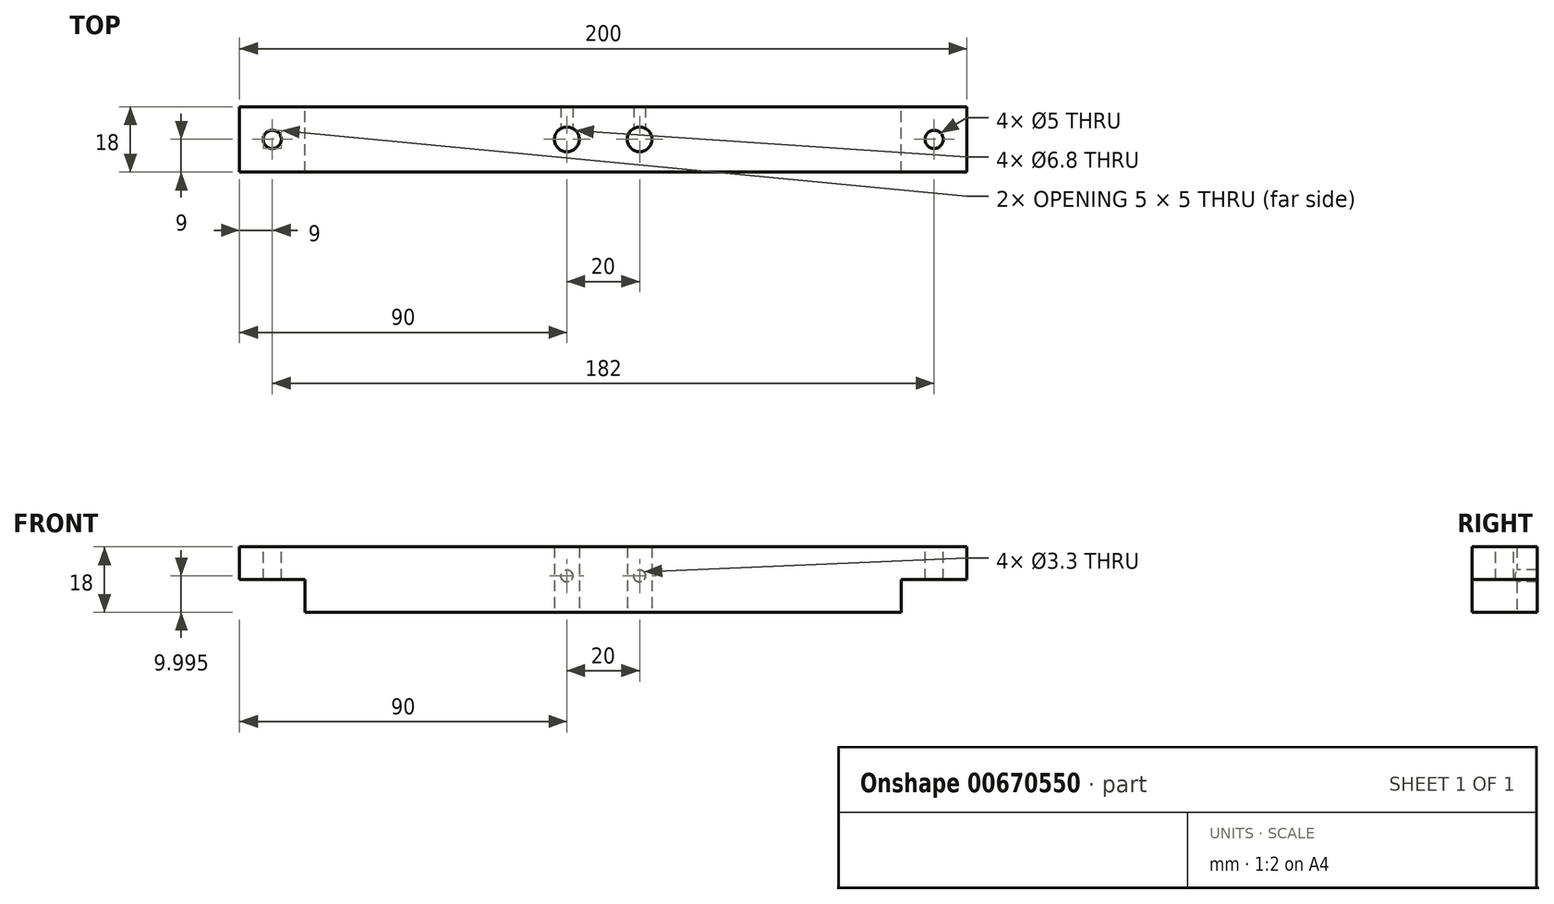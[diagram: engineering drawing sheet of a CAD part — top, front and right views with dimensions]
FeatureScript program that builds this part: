
annotation { "Feature Type Name" : "Feature", "Feature Type Description" : "" }
export const myFeature = defineFeature(function(context is Context, id is Id, definition is map)
    precondition{}
    {
        {
            var Q0;
            Q0=qCreatedBy(makeId("Right.planeOp"),FACE);
            var sketch = newSketch(context, id + "F0", { "sketchPlane" : qUnion([Q0])});
            skLineSegment(sketch, "E0.bottom", {"start": v(5.9, 10.36) * mm, "end": v(-12.1, 10.36) * mm});
            skLineSegment(sketch, "E0.top", {"start": v(5.9, -7.64) * mm, "end": v(-12.1, -7.64) * mm});
            skLineSegment(sketch, "E0.left", {"start": v(5.9, 10.36) * mm, "end": v(5.9, -7.64) * mm});
            skLineSegment(sketch, "E0.right", {"start": v(-12.1, 10.36) * mm, "end": v(-12.1, -7.64) * mm});
            skSolve(sketch);
        }
        {
            var Q0;
            Q0=makeQuery(id+"F0.imprint","IMPRINT",FACE,{"disambiguationData":[TD([[makeQuery(id+"F0.imprint","IMPRINT",EDGE,{"derivedFrom":sQuery(id+"F0.wireOp",EDGE,"E0.bottom")}),1.0]])]});
            extrude(context, id + "F1", {"entities" : qUnion([Q0]), "depth" : 200 * mm, "offsetDistance" : 25 * mm, "symmetric" : true});
        }
        {
            var Q0;
            Q0=makeQuery(id+"F1.opExtrude","SWEPT_FACE",FACE,{"disambiguationData":[OSD([sQuery(id+"F0.wireOp",EDGE,"E0.bottom")])]});
            var sketch = newSketch(context, id + "F2", { "sketchPlane" : qUnion([Q0])});
            skPoint(sketch, "E1", {"position": v(-10, -3.1) * mm});
            skPoint(sketch, "E2", {"position": v(10, -3.1) * mm});
            skSolve(sketch);
        }
        {
            var Q0;
            Q0=sQuery(id+"F2.wireOp",VERTEX,"E1");
            var Q1;
            Q1=sQuery(id+"F2.wireOp",VERTEX,"E2");
            var Q2;
            Q2=makeQuery(id+"F1.opExtrude","SWEPT_BODY",BODY,{"disambiguationData":[OSD([sQuery(id+"F0.wireOp",EDGE,"E0.bottom"),sQuery(id+"F0.wireOp",EDGE,"E0.top"),sQuery(id+"F0.wireOp",EDGE,"E0.left"),sQuery(id+"F0.wireOp",EDGE,"E0.right")])]});
            hole(context, id + "F3", {"style" : HoleStyle.SIMPLE, "endStyle" : HoleEndStyle.THROUGH, "standardTappedOrClearance" : lookupTablePath({ "standard" : "ISO", "engagement" : "75%", "pitch" : "1.25 mm", "size" : "M8", "type" : "Tapped" }), "standardBlindInLast" : lookupTablePath({ "standard" : "ISO", "engagement" : "75%", "pitch" : "1.25 mm", "size" : "M8", "type" : "Tapped" }), "holeDiameter" : 6.8 * mm, "majorDiameter" : 8 * mm, "showTappedDepth" : true, "isTappedThrough" : true, "tappedDepth" : 10 * mm, "tapClearance" : 3, "locations" : qUnion([Q0, Q1]), "scope" : qUnion([Q2]), "startStyle" : HoleStartStyle.PART});
        }
        {
            var Q0;
            Q0=makeQuery(id+"F1.opExtrude","SWEPT_FACE",FACE,{"disambiguationData":[OSD([sQuery(id+"F0.wireOp",EDGE,"E0.left")])]});
            var sketch = newSketch(context, id + "F4", { "sketchPlane" : qUnion([Q0])});
            skPoint(sketch, "E3", {"position": v(-10, 2.36) * mm});
            skPoint(sketch, "E4", {"position": v(10, 2.36) * mm});
            skSolve(sketch);
        }
        {
            var Q0;
            Q0=sQuery(id+"F4.wireOp",VERTEX,"E3");
            var Q1;
            Q1=sQuery(id+"F4.wireOp",VERTEX,"E4");
            var Q2;
            Q2=makeQuery(id+"F1.opExtrude","SWEPT_BODY",BODY,{"disambiguationData":[OSD([sQuery(id+"F0.wireOp",EDGE,"E0.bottom"),sQuery(id+"F0.wireOp",EDGE,"E0.top"),sQuery(id+"F0.wireOp",EDGE,"E0.left"),sQuery(id+"F0.wireOp",EDGE,"E0.right")])]});
            hole(context, id + "F5", {"style" : HoleStyle.SIMPLE, "endStyle" : HoleEndStyle.BLIND, "standardTappedOrClearance" : lookupTablePath({ "standard" : "ISO", "engagement" : "75%", "pitch" : "0.7 mm", "size" : "M4", "type" : "Tapped" }), "standardBlindInLast" : lookupTablePath({ "standard" : "ISO", "engagement" : "75%", "pitch" : "0.7 mm", "size" : "M4", "type" : "Tapped" }), "holeDiameter" : 3.3 * mm, "majorDiameter" : 4 * mm, "showTappedDepth" : true, "holeDepth" : 8 * mm, "isTappedThrough" : true, "tappedDepth" : 5.9 * mm, "tapClearance" : 3, "locations" : qUnion([Q0, Q1]), "scope" : qUnion([Q2]), "startStyle" : HoleStartStyle.PART});
        }
        {
            var Q0;
            Q0=makeQuery(id+"F1.opExtrude","SWEPT_FACE",FACE,{"disambiguationData":[OSD([sQuery(id+"F0.wireOp",EDGE,"E0.bottom")])]});
            var sketch = newSketch(context, id + "F6", { "sketchPlane" : qUnion([Q0])});
            skLineSegment(sketch, "E5.bottom", {"start": v(112, -12.1) * mm, "end": v(100, -12.1) * mm});
            skLineSegment(sketch, "E5.top", {"start": v(112, 5.9) * mm, "end": v(100, 5.9) * mm});
            skLineSegment(sketch, "E5.left", {"start": v(100, -12.1) * mm, "end": v(100, 5.9) * mm});
            skLineSegment(sketch, "E6.bottom", {"start": v(-100, -12.1) * mm, "end": v(-112, -12.1) * mm});
            skLineSegment(sketch, "E6.top", {"start": v(-100, 5.9) * mm, "end": v(-112, 5.9) * mm});
            skLineSegment(sketch, "E6.right", {"start": v(-100, -12.1) * mm, "end": v(-100, 5.9) * mm});
            skSolve(sketch);
        }
        {
            var Q0;
            Q0=makeQuery(id+"F1.opExtrude","SWEPT_FACE",FACE,{"disambiguationData":[OSD([sQuery(id+"F0.wireOp",EDGE,"E0.top")])]});
            var sketch = newSketch(context, id + "F7", { "sketchPlane" : qUnion([Q0])});
            skLineSegment(sketch, "E7.bottom", {"start": v(-100, 12.1) * mm, "end": v(-82, 12.1) * mm});
            skLineSegment(sketch, "E7.top", {"start": v(-100, -5.9) * mm, "end": v(-82, -5.9) * mm});
            skLineSegment(sketch, "E7.left", {"start": v(-100, 12.1) * mm, "end": v(-100, -5.9) * mm});
            skLineSegment(sketch, "E7.right", {"start": v(-82, 12.1) * mm, "end": v(-82, -5.9) * mm});
            skLineSegment(sketch, "E8.bottom", {"start": v(82, 12.1) * mm, "end": v(100, 12.1) * mm});
            skLineSegment(sketch, "E8.top", {"start": v(82, -5.9) * mm, "end": v(100, -5.9) * mm});
            skLineSegment(sketch, "E8.left", {"start": v(82, 12.1) * mm, "end": v(82, -5.9) * mm});
            skLineSegment(sketch, "E8.right", {"start": v(100, 12.1) * mm, "end": v(100, -5.9) * mm});
            skPoint(sketch, "E9", {"position": v(91, 3.1) * mm});
            skPoint(sketch, "E10", {"position": v(-91, 3.1) * mm});
            skSolve(sketch);
        }
        {
            var Q0;
            Q0=sQuery(id+"F7.wireOp",VERTEX,"E9");
            var Q1;
            Q1=sQuery(id+"F7.wireOp",VERTEX,"E10");
            var Q2;
            Q2=makeQuery(id+"F1.opExtrude","SWEPT_BODY",BODY,{"disambiguationData":[OSD([sQuery(id+"F0.wireOp",EDGE,"E0.bottom"),sQuery(id+"F0.wireOp",EDGE,"E0.top"),sQuery(id+"F0.wireOp",EDGE,"E0.left"),sQuery(id+"F0.wireOp",EDGE,"E0.right")])]});
            hole(context, id + "F8", {"style" : HoleStyle.SIMPLE, "endStyle" : HoleEndStyle.BLIND, "standardTappedOrClearance" : lookupTablePath({ "standard" : "ISO", "engagement" : "75%", "pitch" : "1 mm", "size" : "M6", "type" : "Tapped" }), "standardBlindInLast" : lookupTablePath({ "standard" : "ISO", "engagement" : "75%", "pitch" : "1 mm", "size" : "M6", "type" : "Tapped" }), "holeDiameter" : 5 * mm, "majorDiameter" : 6 * mm, "showTappedDepth" : true, "holeDepth" : 18 * mm, "isTappedThrough" : true, "tappedDepth" : 15 * mm, "tapClearance" : 3, "locations" : qUnion([Q0, Q1]), "scope" : qUnion([Q2]), "startStyle" : HoleStartStyle.PART});
        }
        {
            var Q0;
            Q0=makeQuery(id+"F7.imprint","IMPRINT",FACE,{"disambiguationData":[TD([[makeQuery(id+"F7.imprint","IMPRINT",EDGE,{"derivedFrom":sQuery(id+"F7.wireOp",EDGE,"E7.bottom")}),1.0]])]});
            var Q1;
            Q1=makeQuery(id+"F7.imprint","IMPRINT",FACE,{"disambiguationData":[TD([[makeQuery(id+"F7.imprint","IMPRINT",EDGE,{"derivedFrom":sQuery(id+"F7.wireOp",EDGE,"E8.bottom")}),1.0]])]});
            extrude(context, id + "F9", {"entities" : qUnion([Q0, Q1]), "operationType" : NewBodyOperationType.REMOVE, "oppositeDirection" : true, "depth" : 9 * mm, "offsetDistance" : 25 * mm});
        }
    });
